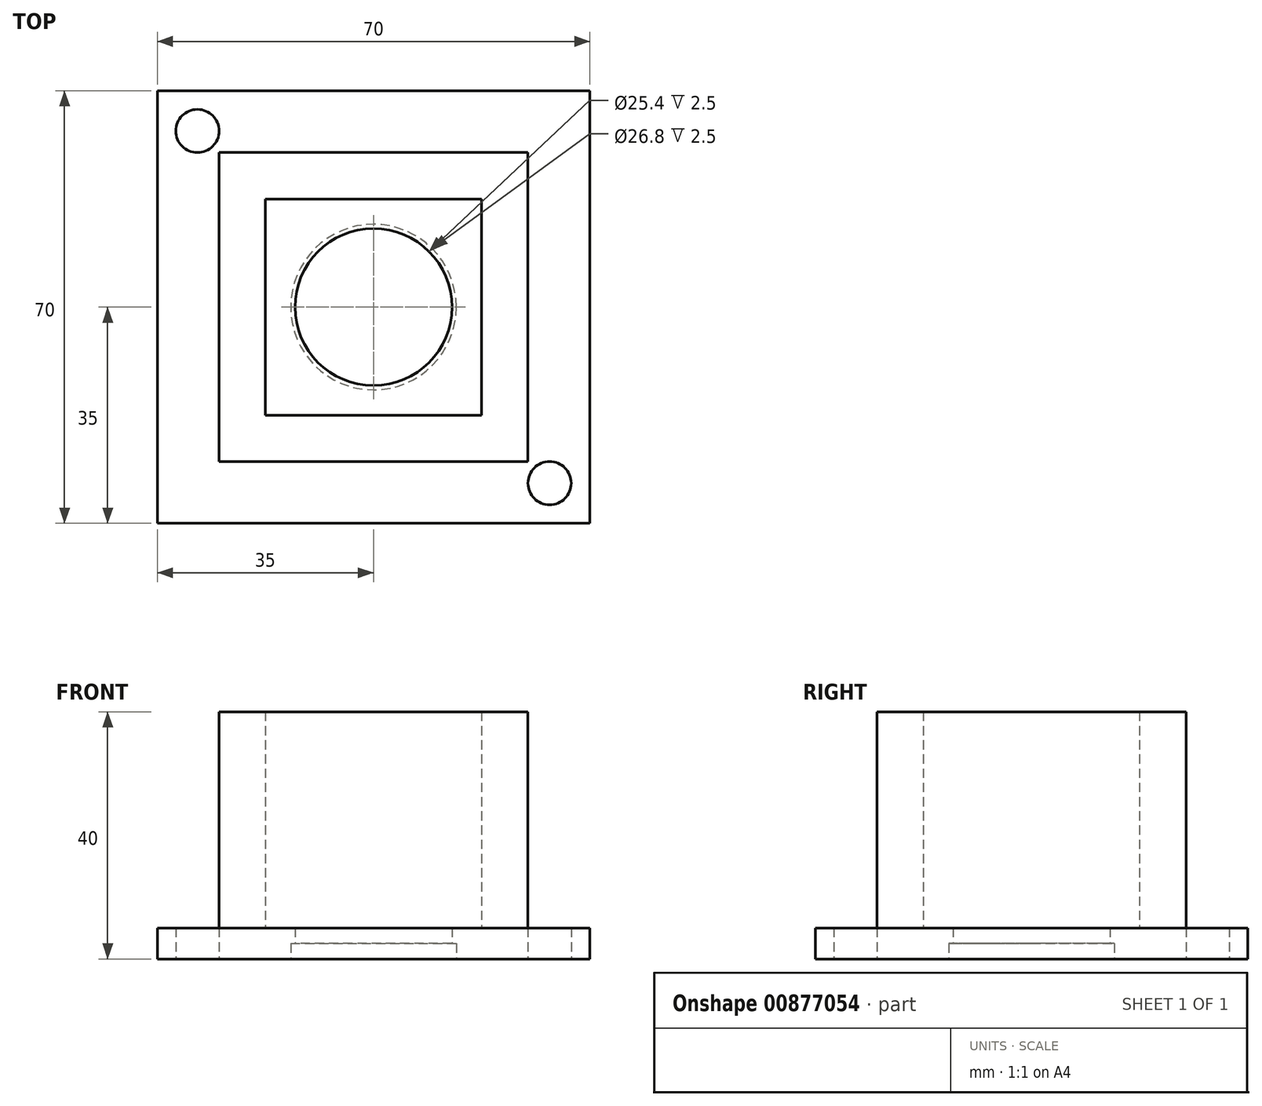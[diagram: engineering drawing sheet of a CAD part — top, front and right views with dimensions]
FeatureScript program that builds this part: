
annotation { "Feature Type Name" : "Feature", "Feature Type Description" : "" }
export const myFeature = defineFeature(function(context is Context, id is Id, definition is map)
    precondition{}
    {
        {
            var Q0;
            Q0=qCreatedBy(makeId("Top.planeOp"),FACE);
            var sketch = newSketch(context, id + "F0", { "sketchPlane" : qUnion([Q0])});
            skLineSegment(sketch, "E0.bottom", {"start": v(-35, 35) * mm, "end": v(35, 35) * mm});
            skLineSegment(sketch, "E0.top", {"start": v(-35, -35) * mm, "end": v(35, -35) * mm});
            skLineSegment(sketch, "E0.left", {"start": v(-35, 35) * mm, "end": v(-35, -35) * mm});
            skLineSegment(sketch, "E0.right", {"start": v(35, 35) * mm, "end": v(35, -35) * mm});
            skPoint(sketch, "E0.middle", {"position": v(0, 0) * mm});
            skCircle(sketch, "E1", {"center": v(0, 0) * mm, "radius": 12.7 * mm});
            skCircle(sketch, "E2", {"center": v(-28.5, 28.5) * mm, "radius": 3.5 * mm});
            skCircle(sketch, "E3", {"center": v(28.5, -28.5) * mm, "radius": 3.5 * mm});
            skSolve(sketch);
        }
        {
            var Q0;
            Q0=makeQuery(id+"F0.imprint","IMPRINT",FACE,{"disambiguationData":[TD([[makeQuery(id+"F0.imprint","IMPRINT",EDGE,{"derivedFrom":sQuery(id+"F0.wireOp",EDGE,"E0.bottom")}),-1.0]])]});
            var Q1;
            Q1 = qSketchRegion(id + "F2", true);
            extrude(context, id + "F1", {"entities" : qUnion([Q0, Q1]), "depth" : 5 * mm, "offsetDistance" : 25 * mm});
        }
        {
            var Q0;
            Q0=makeQuery(id+"F1.opExtrude","CAP_FACE",FACE,{"disambiguationData":[OSD([sQuery(id+"F0.wireOp",EDGE,"E0.bottom"),sQuery(id+"F0.wireOp",EDGE,"E0.top"),sQuery(id+"F0.wireOp",EDGE,"E0.left"),sQuery(id+"F0.wireOp",EDGE,"E0.right"),sQuery(id+"F0.wireOp",EDGE,"E1"),sQuery(id+"F0.wireOp",EDGE,"E2"),sQuery(id+"F0.wireOp",EDGE,"E3")])],"isStart":false});
            var sketch = newSketch(context, id + "F2", { "sketchPlane" : qUnion([Q0])});
            skLineSegment(sketch, "E4.bottom", {"start": v(-25, 25) * mm, "end": v(25, 25) * mm});
            skLineSegment(sketch, "E4.top", {"start": v(-25, -25) * mm, "end": v(25, -25) * mm});
            skLineSegment(sketch, "E4.left", {"start": v(-25, 25) * mm, "end": v(-25, -25) * mm});
            skLineSegment(sketch, "E4.right", {"start": v(25, 25) * mm, "end": v(25, -25) * mm});
            skPoint(sketch, "E4.middle", {"position": v(0, 0) * mm});
            skLineSegment(sketch, "E5.bottom", {"start": v(-17.5, 17.5) * mm, "end": v(17.5, 17.5) * mm});
            skLineSegment(sketch, "E5.top", {"start": v(-17.5, -17.5) * mm, "end": v(17.5, -17.5) * mm});
            skLineSegment(sketch, "E5.left", {"start": v(-17.5, 17.5) * mm, "end": v(-17.5, -17.5) * mm});
            skLineSegment(sketch, "E5.right", {"start": v(17.5, 17.5) * mm, "end": v(17.5, -17.5) * mm});
            skSolve(sketch);
        }
        {
            var Q0;
            Q0=makeQuery(id+"F2.imprint","IMPRINT",FACE,{"disambiguationData":[TD([[makeQuery(id+"F2.imprint","IMPRINT",EDGE,{"derivedFrom":sQuery(id+"F2.wireOp",EDGE,"E4.bottom")}),-1.0]])]});
            extrude(context, id + "F3", {"entities" : qUnion([Q0]), "operationType" : NewBodyOperationType.ADD, "depth" : 35 * mm, "offsetDistance" : 25 * mm});
        }
        {
            var Q0;
            Q0=makeQuery(id+"F1.opExtrude","CAP_FACE",FACE,{"disambiguationData":[OSD([sQuery(id+"F0.wireOp",EDGE,"E0.bottom"),sQuery(id+"F0.wireOp",EDGE,"E0.top"),sQuery(id+"F0.wireOp",EDGE,"E0.left"),sQuery(id+"F0.wireOp",EDGE,"E0.right"),sQuery(id+"F0.wireOp",EDGE,"E1"),sQuery(id+"F0.wireOp",EDGE,"E2"),sQuery(id+"F0.wireOp",EDGE,"E3")])],"isStart":true});
            var sketch = newSketch(context, id + "F4", { "sketchPlane" : qUnion([Q0])});
            skCircle(sketch, "E6", {"center": v(0, 0) * mm, "radius": 13.4 * mm});
            skSolve(sketch);
        }
        {
            var Q0;
            Q0=makeQuery(id+"F4.imprint","IMPRINT",FACE,{"disambiguationData":[TD([[makeQuery(id+"F4.imprint","IMPRINT",EDGE,{"derivedFrom":sQuery(id+"F4.wireOp",EDGE,"E6")}),1.0]])]});
            extrude(context, id + "F5", {"entities" : qUnion([Q0]), "operationType" : NewBodyOperationType.REMOVE, "oppositeDirection" : true, "depth" : 2.5 * mm, "offsetDistance" : 25 * mm});
        }
    });
